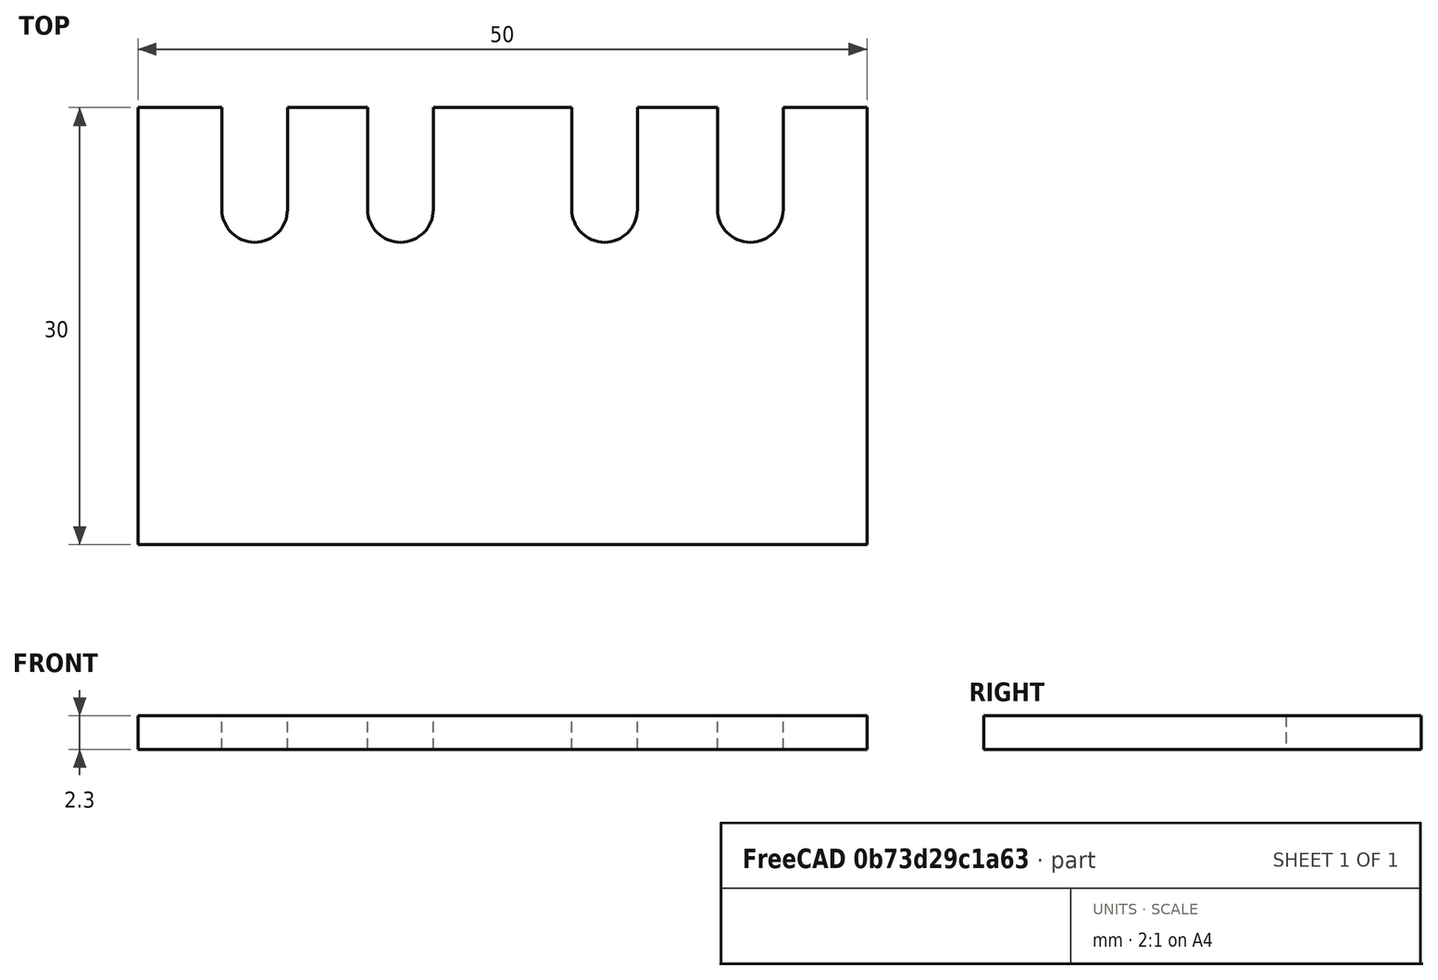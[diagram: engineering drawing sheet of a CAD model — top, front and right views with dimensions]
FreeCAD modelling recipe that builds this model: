
FCSTD DOCUMENT  (FreeCAD 0.19R24291 (Git))
Label: ResponseBox_testPlate2
License: All rights reserved
LicenseURL: http://en.wikipedia.org/wiki/All_rights_reserved
objects: Sketcher::SketchObject×1, PartDesign::Pad×1, PartDesign::Body×1
note: 4 computed .brp shape members not serialized (recipe doc carries the construction recipe); baked Part::Feature solids carry a one-line shape summary decoded from their .brp

FEATURE [Sketcher::SketchObject] Sketch
  FullyConstrained = true
  MapMode = 5
  Support = -> [XY_Plane]
  sketch-geometry (20):
    g0: LineSegment StartX=0 StartY=0 StartZ=0 EndX=50 EndY=0 EndZ=0
    g1: LineSegment StartX=50 StartY=0 StartZ=0 EndX=50 EndY=30 EndZ=0
    g2: LineSegment StartX=0 StartY=30 StartZ=0 EndX=0 EndY=0 EndZ=0
    g3: ArcOfCircle CenterX=8 CenterY=23 CenterZ=0 NormalX=0 NormalY=0 NormalZ=1 AngleXU=0 Radius=2.25 StartAngle=3.14159 EndAngle=6.28319
    g4: ArcOfCircle CenterX=18 CenterY=23 CenterZ=0 NormalX=0 NormalY=0 NormalZ=1 AngleXU=0 Radius=2.25 StartAngle=3.14159 EndAngle=6.28319
    g5: ArcOfCircle CenterX=32 CenterY=23 CenterZ=0 NormalX=0 NormalY=0 NormalZ=1 AngleXU=0 Radius=2.25 StartAngle=3.14159 EndAngle=6.28319
    g6: ArcOfCircle CenterX=42 CenterY=23 CenterZ=0 NormalX=0 NormalY=0 NormalZ=1 AngleXU=0 Radius=2.25 StartAngle=3.14159 EndAngle=6.28319
    g7: LineSegment StartX=10.25 StartY=30 StartZ=0 EndX=10.25 EndY=23 EndZ=0
    g8: LineSegment StartX=5.75 StartY=23 StartZ=0 EndX=5.75 EndY=30 EndZ=0
    g9: LineSegment StartX=20.25 StartY=30 StartZ=0 EndX=20.25 EndY=23 EndZ=0
    g10: LineSegment StartX=15.75 StartY=23 StartZ=0 EndX=15.75 EndY=30 EndZ=0
    g11: LineSegment StartX=34.25 StartY=30 StartZ=0 EndX=34.25 EndY=23 EndZ=0
    g12: LineSegment StartX=29.75 StartY=23 StartZ=0 EndX=29.75 EndY=30 EndZ=0
    g13: LineSegment StartX=44.25 StartY=30 StartZ=0 EndX=44.25 EndY=23 EndZ=0
    g14: LineSegment StartX=39.75 StartY=23 StartZ=0 EndX=39.75 EndY=30 EndZ=0
    g15: LineSegment StartX=5.75 StartY=30 StartZ=0 EndX=0 EndY=30 EndZ=0
    g16: LineSegment StartX=15.75 StartY=30 StartZ=0 EndX=10.25 EndY=30 EndZ=0
    g17: LineSegment StartX=29.75 StartY=30 StartZ=0 EndX=20.25 EndY=30 EndZ=0
    g18: LineSegment StartX=39.75 StartY=30 StartZ=0 EndX=34.25 EndY=30 EndZ=0
    g19: LineSegment StartX=44.25 StartY=30 StartZ=0 EndX=50 EndY=30 EndZ=0
  constraints (63):
    c: Coincident(g0,g1)
    c: Coincident(g15,g2)
    c: Coincident(g2,g0)
    c: Horizontal(g0)
    c: Vertical(g1)
    c: Vertical(g2)
    c: DistanceX(g15,g1) = 50
    c: DistanceY(g2,g2) = 30
    c: Coincident(g0,g-1)
    c: Radius(g3) = 2.25
    c: Radius(g4) = 2.25
    c: Radius(g5) = 2.25
    c: Radius(g6) = 2.25
    c: DistanceX(g3,g4) = 10
    c: DistanceX(g5,g6) = 10
    c: DistanceY(g4,g3) = 0
    c: DistanceY(g5,g6) = 0
    c: DistanceY(g3,g15) = 7
    c: DistanceY(g5,g4) = 0
    c: DistanceX(g15,g3) = 8
    c: DistanceX(g6,g1) = 8
    c: Vertical(g7)
    c: Vertical(g8)
    c: Vertical(g9)
    c: Vertical(g10)
    c: Vertical(g11)
    c: Vertical(g12)
    c: Vertical(g13)
    c: Vertical(g14)
    c: DistanceY(g3,g7) = 0
    c: DistanceY(g4,g9) = 0
    c: DistanceY(g5,g11) = 0
    c: DistanceY(g6,g13) = 0
    c: DistanceY(g13,g1) = 0
    c: DistanceY(g11,g14) = 0
    c: DistanceY(g7,g10) = 0
    c: Coincident(g3,g7)
    c: Coincident(g4,g9)
    c: Coincident(g5,g11)
    c: Coincident(g6,g13)
    c: Coincident(g3,g8)
    c: Coincident(g4,g10)
    c: Coincident(g5,g12)
    c: Coincident(g6,g14)
    c: DistanceY(g8,g7) = 0
    c: DistanceY(g10,g9) = 0
    c: DistanceY(g11,g12) = 0
    c: DistanceY(g14,g13) = 0
    c: DistanceY(g13,g13) = 7
    c: DistanceY(g14,g14) = 7
    c: DistanceY(g12,g12) = 7
    c: DistanceY(g9,g9) = 7
    c: DistanceY(g10,g10) = 7
    c: DistanceY(g8,g8) = 7
    c: Coincident(g19,g13)
    c: Coincident(g1,g19)
    c: Coincident(g17,g9)
    c: Coincident(g17,g12)
    c: Coincident(g8,g15)
    c: Coincident(g7,g16)
    c: Coincident(g10,g16)
    c: Coincident(g11,g18)
    c: Coincident(g14,g18)
FEATURE [PartDesign::Pad] Pad
  Direction = (1,1,1)
  Length = 2.3
  Length2 = 100
  Profile = -> Sketch
  Type = 0
FEATURE [PartDesign::Body] Body
  Group = -> [Sketch,Pad]
  Origin = -> Origin
  Tip = -> Pad
